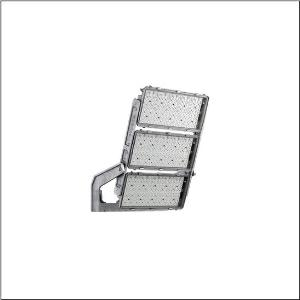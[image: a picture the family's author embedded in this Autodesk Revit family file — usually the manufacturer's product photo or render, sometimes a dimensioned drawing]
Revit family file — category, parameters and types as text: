
# Revit family: floodlight_fl_11_maxi_pro_remote___pl33t_5xa779425t01aa_7d4a
name_source: partatom
category: Lighting Fixtures
units: mm (PartAtom-declared; Revit-internal decimal feet)

## family parameters
Cut with Voids When Loaded = No
Host = Face
Light Source = No
Part Type = Normal
Room Calculation Point = No
Round Connector Dimension = Use Diameter
Shared = No

## types (1)
- --- (1 x LED, 201910 lm, 1539.3 W, 3000K)
    Apparent Load = 1539 VA
    CIE Flux Codes = 27 70 98 100 100
    Color Rendering = 70
    Color Temperature = 3000K
    Default Elevation = 1800 mm
    Description = Floodlight FL 11  maxi  pro Remote floodlight; light control with lens of PMMA; cover panel of toughened safety glass, transparent; light distribution: PL33T, asymmetric direct distribution, LEDcolour temperature: 3000K, rated luminous flux: 201.910lm, colour rendering: CRI > 70, light colour: 730; luminous efficacy: 131lm/W; brightness control: DALI 2 (1 DALI address); with terminal, 8-pole, max. 2.5mm², mains connection: 220..240V/380..400V AC, 50/60Hz, surge voltage resistance: line to ground: 10kV, ECG replaceable separately, no afterglow with DALI off / DMX off command, LED unit replaceable without ESD environment, dustproof LED module, dimming range 10..100%; 1539W floodlight with 2x LED unit of diecast aluminium, coated grey; length: 713mm / width: 651mm / height: 338mm; mounting bracket, of diecast aluminium, uncoated, natural, equipment: Power, protection rating (complete): IP66; insulation class (complete): insulation class I (protective earthing); certification: CE, ENEC, VDE; ball protection: ball impact resistance with accessories, impact resistance: IK07; only for outdoor installations, rated ambient temperature 10°C, permissible operating ambient temperature: -40..+30°C, permissible storage temperature: -40..+85°C; packaging unit: 1 piece

Light Distribution: PL33T
    Height = 320 mm
    Lamp = 1 x LED
    Lamp Light Flux = 201910 lm
    Lamp Power = 1539.3 W
    Lamp count = 1
    Length = 1002 mm
    Luminous efficacy = 131 lm/W
    Manufacturer = Siteco
    ModVariant = No
    Model = 5XA779425T01AA
    Mounting Place = Ceiling
    Mounting Type = Surface mounted
    Number of Poles = 1
    OnlyDefault = Yes
    Power Factor = 1
    Product Name = Floodlight FL 11 maxi pro Remote | PL33T
    Product group = floodlight | ceiling mounted
    ProductGroupID = 303
    Protection Class = Protection class I
    Protection Degree = IP 66
    RLX_Detail_Level = 1
    RLX_Emergency_Light_Flux = 0 lm
    RLX_Emergency_Type = 0
    RLX_Emergency_Type_DB = No
    RlxData = <blob elided: 52417 chars, md5=c38b4599>
    Socket = socket
    Standby Power = 0 W
    System Light Flux = 201910 lm
    System Power = 1539 W
    Type Comments = factory setting: luminous flux: 100 % | dim-lin: 254 | 1080 mA
    Type Image = l_1006784.jpg
    URL = http://relux.com
    VarID = @adj_030623
    Voltage = 0 V
    Weight = 0.00 kg
    Width = 655 mm

## geometry (parser evidence)
native form markers: Blend x4, Sweep x11
no freeform markers — native parametric forms only
